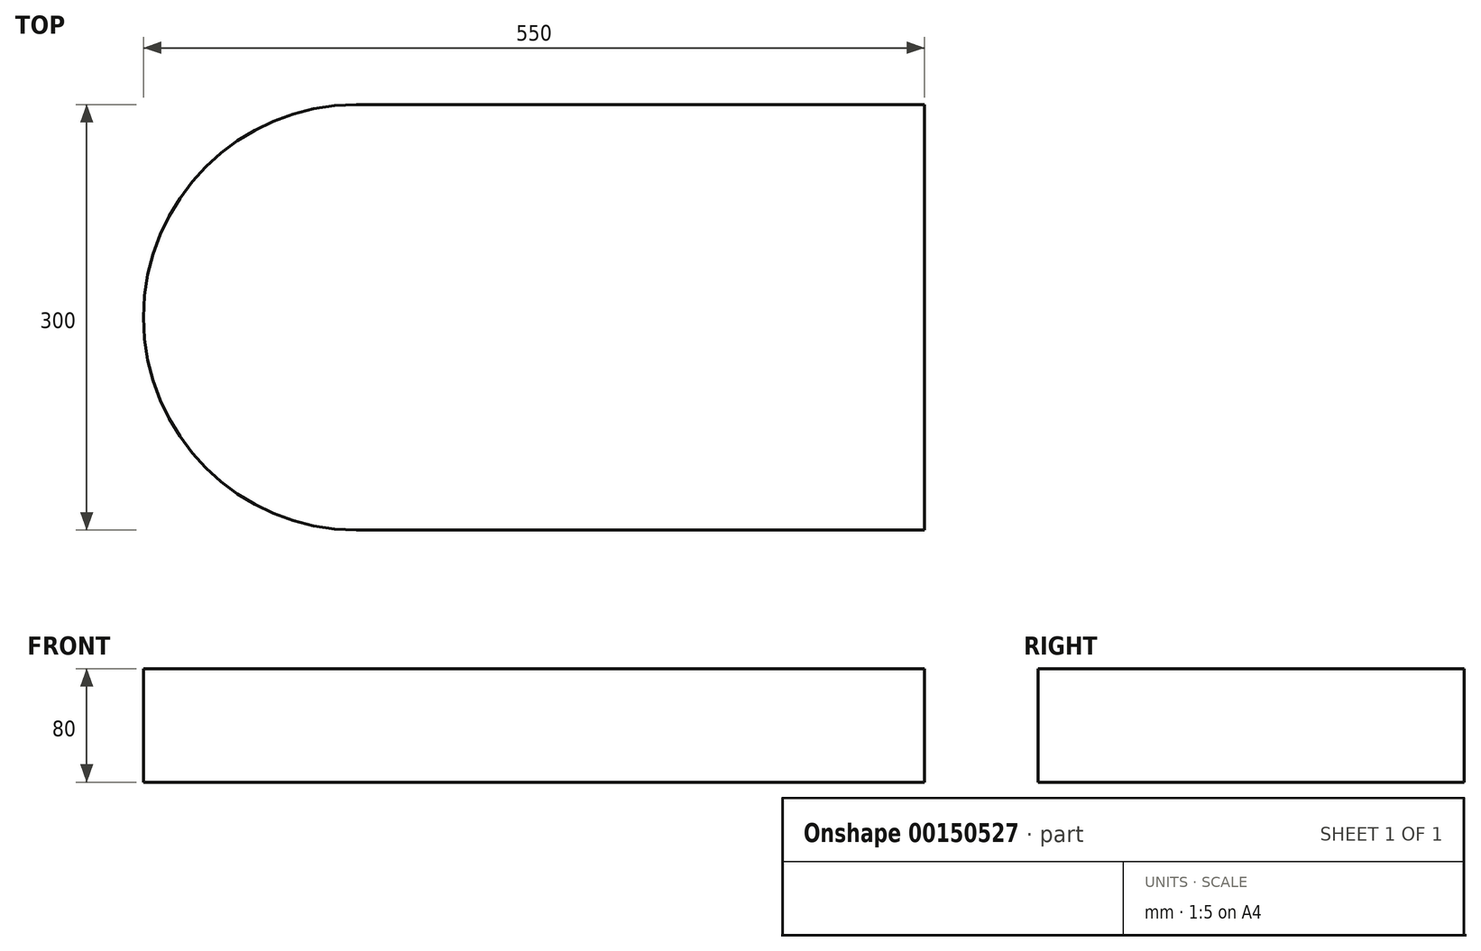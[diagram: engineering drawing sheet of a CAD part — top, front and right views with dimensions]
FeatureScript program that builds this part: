
annotation { "Feature Type Name" : "Feature", "Feature Type Description" : "" }
export const myFeature = defineFeature(function(context is Context, id is Id, definition is map)
    precondition{}
    {
        {
            var Q0;
            Q0=qCreatedBy(makeId("Top.planeOp"),FACE);
            var sketch = newSketch(context, id + "F0", { "sketchPlane" : qUnion([Q0])});
            skLineSegment(sketch, "E0.bottom", {"start": v(200, -150) * mm, "end": v(-200, -150) * mm});
            skLineSegment(sketch, "E0.top", {"start": v(200, 150) * mm, "end": v(-200, 150) * mm});
            skLineSegment(sketch, "E0.left", {"start": v(200, -150) * mm, "end": v(200, 150) * mm});
            skLineSegment(sketch, "E0.right", {"start": v(-200, -150) * mm, "end": v(-200, 150) * mm});
            skPoint(sketch, "E0.middle", {"position": v(0, 0) * mm});
            skCircle(sketch, "E1", {"center": v(-200, 0) * mm, "radius": 150 * mm});
            skSolve(sketch);
        }
        {
            var Q0;
            Q0 = qSketchRegion(id + "F0", true);
            extrude(context, id + "F1", {"entities" : qUnion([Q0]), "depth" : 80 * mm});
        }
    });
